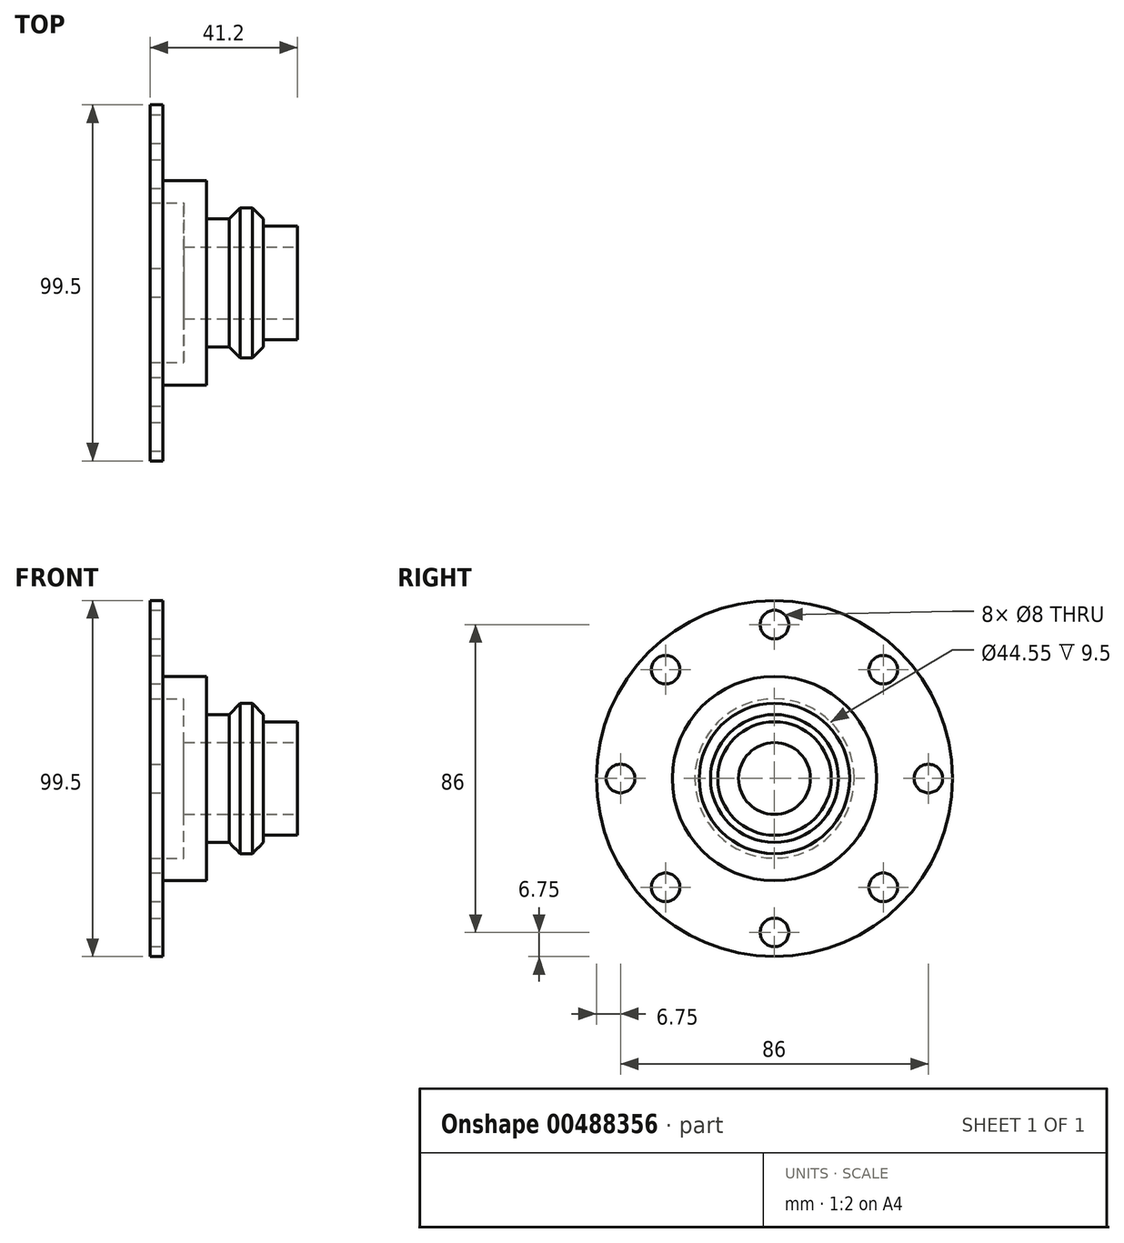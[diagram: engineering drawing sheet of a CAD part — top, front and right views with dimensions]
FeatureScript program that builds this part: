
annotation { "Feature Type Name" : "Feature", "Feature Type Description" : "" }
export const myFeature = defineFeature(function(context is Context, id is Id, definition is map)
    precondition{}
    {
        {
            var Q0;
            Q0=qCreatedBy(makeId("Front.planeOp"),FACE);
            var sketch = newSketch(context, id + "F0", { "sketchPlane" : qUnion([Q0])});
            skLineSegment(sketch, "E0", {"start": v(0, 0) * mm, "end": v(-41.2, 0) * mm, "construction": true});
            skLineSegment(sketch, "E1", {"start": v(-41.2, 0) * mm, "end": v(-41.2, 49.75) * mm, "construction": true});
            skLineSegment(sketch, "E2", {"start": v(0, 0) * mm, "end": v(0, 10.03) * mm, "construction": true});
            skLineSegment(sketch, "E3", {"start": v(0, 10.03) * mm, "end": v(0, 15.85) * mm});
            skLineSegment(sketch, "E4", {"start": v(0, 15.85) * mm, "end": v(-9.5, 15.85) * mm});
            skLineSegment(sketch, "E5", {"start": v(-9.5, 15.85) * mm, "end": v(-9.5, 17.88) * mm});
            skLineSegment(sketch, "E6", {"start": v(-9.5, 17.88) * mm, "end": v(-12.62, 21) * mm});
            skLineSegment(sketch, "E7", {"start": v(-12.62, 21) * mm, "end": v(-15.98, 21) * mm});
            skLineSegment(sketch, "E8", {"start": v(-15.98, 21) * mm, "end": v(-19.1, 17.88) * mm});
            skLineSegment(sketch, "E9", {"start": v(-19.1, 17.88) * mm, "end": v(-25.45, 17.88) * mm});
            skLineSegment(sketch, "E10", {"start": v(-25.45, 17.88) * mm, "end": v(-25.45, 28.55) * mm});
            skLineSegment(sketch, "E11", {"start": v(-25.45, 28.55) * mm, "end": v(-37.65, 28.55) * mm});
            skLineSegment(sketch, "E12", {"start": v(-37.65, 28.55) * mm, "end": v(-37.65, 49.75) * mm});
            skLineSegment(sketch, "E13", {"start": v(-37.65, 49.75) * mm, "end": v(-41.2, 49.75) * mm});
            skLineSegment(sketch, "E14", {"start": v(-41.2, 49.75) * mm, "end": v(-41.2, 22.27) * mm});
            skLineSegment(sketch, "E15", {"start": v(-41.2, 22.27) * mm, "end": v(-31.7, 22.27) * mm});
            skLineSegment(sketch, "E16", {"start": v(-31.7, 22.27) * mm, "end": v(-31.7, 10.03) * mm});
            skLineSegment(sketch, "E17", {"start": v(-31.7, 10.03) * mm, "end": v(0, 10.03) * mm});
            skSolve(sketch);
        }
        {
            var Q0;
            Q0 = qSketchRegion(id + "F0", true);
            var Q1;
            Q1=sQuery(id+"F0.wireOp",EDGE,"E0");
            revolve(context, id + "F1", {"entities" : qUnion([Q0]), "axis" : qUnion([Q1]), "revolveType" : RevolveType.FULL});
        }
        {
            var Q0;
            Q0=makeQuery(id+"F1.opRevolve","SWEPT_FACE",FACE,{"disambiguationData":[OSD([sQuery(id+"F0.wireOp",EDGE,"E12")])]});
            var sketch = newSketch(context, id + "F2", { "sketchPlane" : qUnion([Q0])});
            skCircle(sketch, "E18", {"center": v(0, 0) * mm, "radius": 43 * mm, "construction": true});
            skCircle(sketch, "E19", {"center": v(0, 43) * mm, "radius": 4 * mm});
            skCircle(sketch, "E20.1.0", {"center": v(30.4, 30.4) * mm, "radius": 4 * mm});
            skCircle(sketch, "E20.2.0", {"center": v(43, 0) * mm, "radius": 4 * mm});
            skCircle(sketch, "E20.3.0", {"center": v(30.4, -30.4) * mm, "radius": 4 * mm});
            skCircle(sketch, "E20.4.0", {"center": v(0, -43) * mm, "radius": 4 * mm});
            skCircle(sketch, "E20.5.0", {"center": v(-30.4, -30.4) * mm, "radius": 4 * mm});
            skCircle(sketch, "E20.6.0", {"center": v(-43, 0) * mm, "radius": 4 * mm});
            skCircle(sketch, "E20.7.0", {"center": v(-30.4, 30.4) * mm, "radius": 4 * mm});
            skLineSegment(sketch, "E20.anchor1", {"start": v(0, 0) * mm, "end": v(0, 43) * mm, "construction": true});
            skLineSegment(sketch, "E20.anchor2", {"start": v(0, 0) * mm, "end": v(-30.4, 30.4) * mm, "construction": true});
            skLineSegment(sketch, "E21", {"start": v(0, 0) * mm, "end": v(-43, 0) * mm, "construction": true});
            skLineSegment(sketch, "E22", {"start": v(0, 0) * mm, "end": v(-30.4, -30.4) * mm, "construction": true});
            skSolve(sketch);
        }
        {
            var Q0;
            Q0 = qSketchRegion(id + "F2", true);
            extrude(context, id + "F3", {"entities" : qUnion([Q0]), "operationType" : NewBodyOperationType.REMOVE, "endBound" : BoundingType.THROUGH_ALL, "oppositeDirection" : true, "depth" : 25 * mm});
        }
    });
